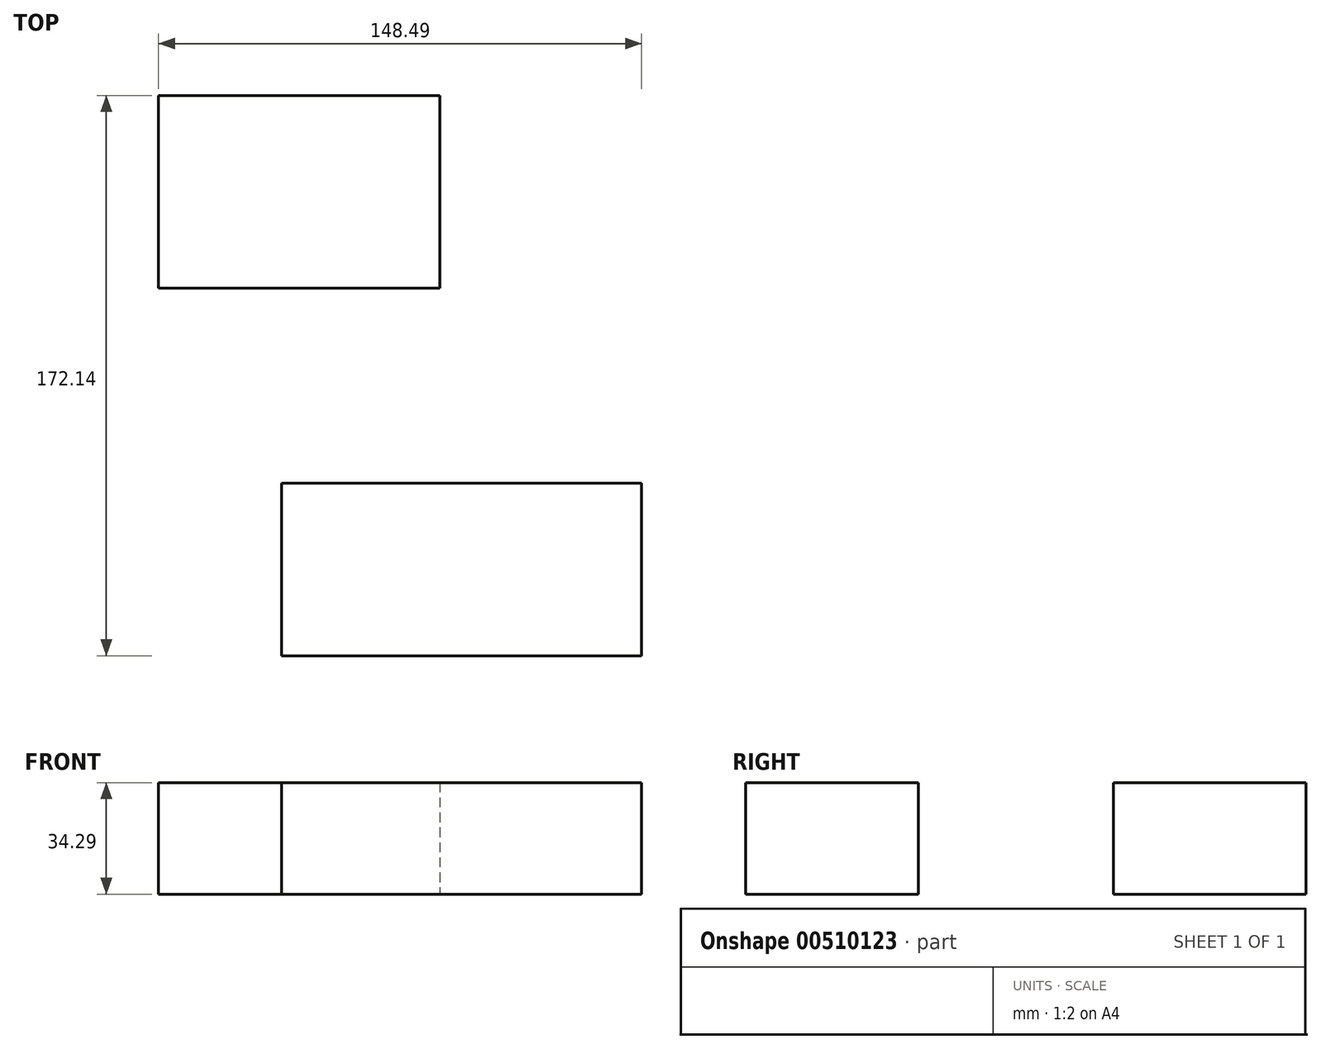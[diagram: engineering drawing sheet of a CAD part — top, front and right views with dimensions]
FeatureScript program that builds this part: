
annotation { "Feature Type Name" : "Feature", "Feature Type Description" : "" }
export const myFeature = defineFeature(function(context is Context, id is Id, definition is map)
    precondition{}
    {
        {
            var Q0;
            Q0=qCreatedBy(makeId("Top.planeOp"),FACE);
            var sketch = newSketch(context, id + "F0", { "sketchPlane" : qUnion([Q0])});
            skLineSegment(sketch, "E0.bottom", {"start": v(-88.4, 41.6) * mm, "end": v(24.84, 41.6) * mm});
            skLineSegment(sketch, "E0.top", {"start": v(-88.4, -48.64) * mm, "end": v(24.84, -48.64) * mm});
            skLineSegment(sketch, "E0.left", {"start": v(-88.4, 41.6) * mm, "end": v(-88.4, -48.64) * mm});
            skLineSegment(sketch, "E0.right", {"start": v(24.84, 41.6) * mm, "end": v(24.84, -48.64) * mm});
            skLineSegment(sketch, "E1.bottom", {"start": v(-56.5, 0) * mm, "end": v(54.22, 0) * mm});
            skLineSegment(sketch, "E1.top", {"start": v(-56.5, -53) * mm, "end": v(54.22, -53) * mm});
            skLineSegment(sketch, "E1.left", {"start": v(-56.5, 0) * mm, "end": v(-56.5, -53) * mm});
            skLineSegment(sketch, "E1.right", {"start": v(54.22, 0) * mm, "end": v(54.22, -53) * mm});
            skLineSegment(sketch, "E2.bottom", {"start": v(-94.27, 119.15) * mm, "end": v(-7.75, 119.15) * mm});
            skLineSegment(sketch, "E2.top", {"start": v(-94.27, 59.95) * mm, "end": v(-7.75, 59.95) * mm});
            skLineSegment(sketch, "E2.left", {"start": v(-94.27, 119.15) * mm, "end": v(-94.27, 59.95) * mm});
            skLineSegment(sketch, "E2.right", {"start": v(-7.75, 119.15) * mm, "end": v(-7.75, 59.95) * mm});
            skSolve(sketch);
        }
        {
            var Q0;
            Q0=makeQuery(id+"F0.imprint","IMPRINT",FACE,{"disambiguationData":[TD([[makeQuery(id+"F0.imprint","IMPRINT",EDGE,{"derivedFrom":sQuery(id+"F0.wireOp",EDGE,"E2.bottom")}),-1.0]])]});
            var Q1;
            {var subQ0=sQuery(id+"F0.wireOp",EDGE,"E1.top");Q1=makeQuery(id+"F0.imprint","IMPRINT",FACE,{"disambiguationData":[TD([[makeQuery(id+"F0.imprint","IMPRINT",EDGE,{"derivedFrom":subQ0}),1.0]])]});}
            var Q2;
            {var subQ0=sQuery(id+"F0.wireOp",EDGE,"E0.right");var subQ1=sQuery(id+"F0.wireOp",EDGE,"E0.top");var subQ2=makeQuery(id+"F0.imprint","INTERSECT",VERTEX,{"derivedFrom":[subQ1,subQ0]});Q2=makeQuery(id+"F0.imprint","IMPRINT",FACE,{"disambiguationData":[TD([[makeQuery(id+"F0.imprint","IMPRINT",EDGE,{"disambiguationData":[TD([[subQ2,1.0]])],"derivedFrom":subQ1}),1.0]])]});}
            extrude(context, id + "F1", {"entities" : qUnion([Q0, Q1, Q2]), "depth" : 34.3 * mm});
        }
    });
